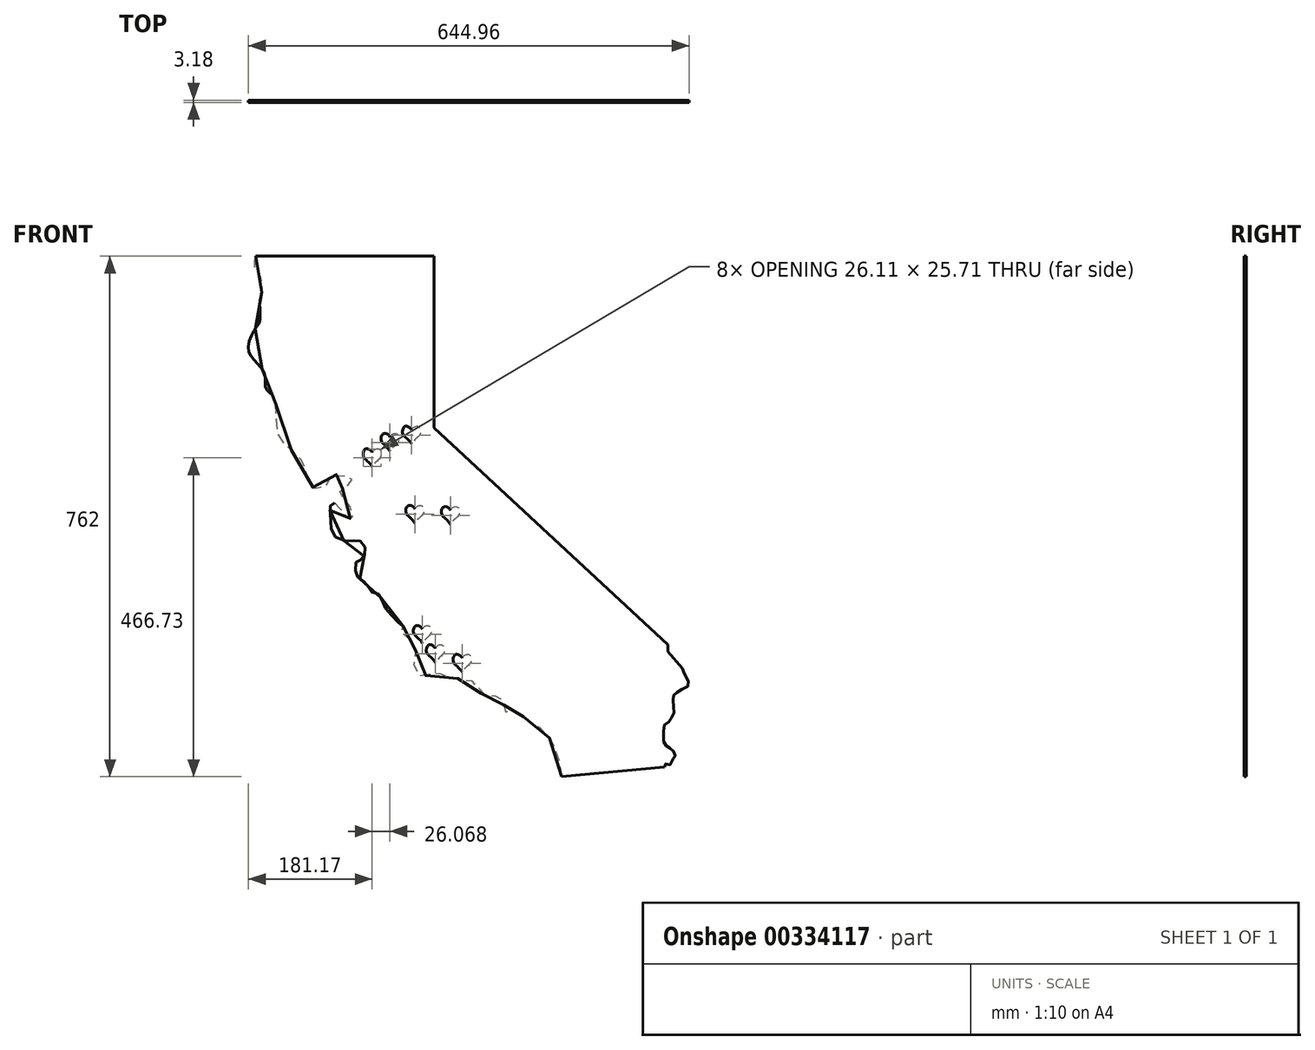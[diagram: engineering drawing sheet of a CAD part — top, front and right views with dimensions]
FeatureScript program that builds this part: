
annotation { "Feature Type Name" : "Feature", "Feature Type Description" : "" }
export const myFeature = defineFeature(function(context is Context, id is Id, definition is map)
    precondition{}
    {
        {
            var Q0;
            Q0=qCreatedBy(makeId("Front.planeOp"),FACE);
            var sketch = newSketch(context, id + "F0", { "sketchPlane" : qUnion([Q0])});
            skPoint(sketch, "E0.middle", {"position": v(0, 0) * mm});
            skLineSegment(sketch, "E1", {"start": v(-635.46, 762) * mm, "end": v(-374.52, 762) * mm});
            skLineSegment(sketch, "E2", {"start": v(-374.52, 762) * mm, "end": v(-374.52, 510.67) * mm});
            skLineSegment(sketch, "E3", {"start": v(-374.52, 510.67) * mm, "end": v(-32.38, 193.27) * mm});
            skLineSegment(sketch, "E4", {"start": v(-32.38, 193.27) * mm, "end": v(-32.38, 183.1) * mm});
            skLineSegment(sketch, "E5", {"start": v(-32.38, 183.1) * mm, "end": v(-11.17, 158.91) * mm});
            skLineSegment(sketch, "E6", {"start": v(-187.52, 0) * mm, "end": v(-37.43, 13.95) * mm});
            skFitSpline(sketch, "E7", {"points": [v(-37.43, 13.95) * mm, v(-37.43, 16.64) * mm, v(-36.79, 17.86) * mm, v(-35.5, 18.8) * mm, v(-33.12, 18.04) * mm, v(-29.91, 17.05) * mm, v(-28.22, 17.8) * mm, v(-27.06, 19.09) * mm, v(-26.77, 21.7) * mm, v(-26.53, 23.34) * mm, v(-25.54, 24.33) * mm, v(-24.32, 25.09) * mm, v(-24.26, 26.31) * mm, v(-23.27, 27.77) * mm, v(-22.16, 28.93) * mm, v(-21.58, 30.1) * mm, v(-21.46, 32.78) * mm, v(-22.16, 34.53) * mm, v(-25.08, 38.78) * mm, v(-27.64, 41.63) * mm, v(-30.38, 42.1) * mm, v(-32.18, 43.9) * mm, v(-34.28, 45.3) * mm, v(-35.62, 45.54) * mm, v(-37.43, 47.52) * mm, v(-38.3, 53.58) * mm, v(-38.36, 67.79) * mm, v(-37.95, 72.92) * mm, v(-36.67, 76.35) * mm, v(-34.46, 78.1) * mm, v(-30.96, 80.08) * mm, v(-28.8, 82.94) * mm, v(-27.99, 85.2) * mm, v(-24.96, 87.6) * mm, v(-23.8, 91.5) * mm, v(-23.21, 97.1) * mm, v(-23.68, 101.23) * mm, v(-24.26, 105.71) * mm, v(-24.55, 111.07) * mm, v(-24.26, 115.27) * mm, v(-23.74, 117.6) * mm, v(-23.62, 119.52) * mm, v(-21.23, 122.67) * mm, v(-18.67, 123.3) * mm, v(-14.53, 127.1) * mm, v(-11.56, 127.97) * mm, v(-5.91, 130.7) * mm, v(-2.24, 132.69) * mm, v(-1.2, 136.42) * mm, v(-3.11, 142.24) * mm, v(-7.83, 150.22) * mm, v(-10.22, 155.3) * mm, v(-11.17, 158.91) * mm], "startDerivative": vector(-13.19, 172.42) * mm, "endDerivative": vector(-38.47, 173.9) * mm});
            skFitSpline(sketch, "E8", {"points": [v(-187.52, 0) * mm, v(-190.53, 20.29) * mm, v(-196.76, 40.63) * mm, v(-204.85, 55.58) * mm, v(-215.23, 67.41) * mm, v(-224.16, 74.68) * mm, v(-237.65, 81.32) * mm, v(-246.16, 91.08) * mm, v(-258.41, 100) * mm, v(-265.68, 93.57) * mm, v(-267.76, 92.74) * mm, v(-271.28, 100.22) * mm, v(-273.98, 113.3) * mm, v(-280.63, 116.62) * mm, v(-293.08, 119.52) * mm, v(-302, 120.15) * mm, v(-307, 124.3) * mm, v(-311.35, 135.92) * mm, v(-320.9, 139.66) * mm, v(-329.83, 139.87) * mm, v(-341.25, 144.23) * mm, v(-355.36, 145.47) * mm, v(-367.82, 151.08) * mm, v(-381.52, 149.63) * mm, v(-389.83, 147.13) * mm, v(-396.88, 148.38) * mm, v(-403.32, 161.87) * mm, v(-401.87, 176.4) * mm, v(-404.57, 195.71) * mm, v(-418.9, 206.72) * mm, v(-420.97, 212.11) * mm, v(-417.85, 214.81) * mm, v(-421.17, 222.08) * mm, v(-426.16, 225.2) * mm, v(-441.52, 241.8) * mm, v(-448.64, 252.16) * mm, v(-454.7, 266.6) * mm, v(-463.56, 268.94) * mm, v(-469.62, 275.46) * mm, v(-472.88, 281.99) * mm, v(-485, 291.3) * mm, v(-488.72, 297.83) * mm, v(-488.72, 313.21) * mm, v(-485, 315.54) * mm, v(-479.4, 318.8) * mm, v(-474.74, 329.06) * mm, v(-478.94, 342.58) * mm, v(-489.2, 345.84) * mm, v(-498.51, 344.44) * mm, v(-520.88, 352.36) * mm, v(-525.54, 369.14) * mm, v(-525.54, 379.4) * mm, v(-526.94, 392.44) * mm, v(-522.75, 401.3) * mm, v(-514.36, 396.64) * mm, v(-508.3, 385.92) * mm, v(-494.78, 378) * mm, v(-496.18, 392.9) * mm, v(-508.3, 408.29) * mm, v(-511.56, 418.08) * mm, v(-495.72, 430.2) * mm, v(-494.78, 435.79) * mm, v(-505.04, 439.51) * mm, v(-514.36, 439.51) * mm, v(-519.48, 443.7) * mm, v(-526, 440.45) * mm, v(-527.87, 433.46) * mm, v(-537.2, 422.27) * mm, v(-555.84, 426.93) * mm, v(-562.83, 451.63) * mm, v(-570.28, 465.61) * mm, v(-591.26, 485.65) * mm, v(-602.44, 501.5) * mm, v(-606.17, 542.98) * mm, v(-611.3, 559.29) * mm, v(-620.62, 568.61) * mm, v(-622.02, 587.72) * mm, v(-635.53, 607.76) * mm, v(-645.95, 624.54) * mm, v(-638.8, 651.1) * mm, v(-629.47, 666.95) * mm, v(-629.47, 688.39) * mm, v(-628.07, 701.9) * mm, v(-626.21, 721.94) * mm, v(-633.2, 740.58) * mm, v(-636.46, 744.31) * mm, v(-635.46, 762) * mm], "startDerivative": vector(-159.4, 1384.08) * mm, "endDerivative": vector(241.74, 1617.9) * mm});
            skSolve(sketch);
        }
        {
            var Q0;
            Q0 = qSketchRegion(id + "F0", true);
            extrude(context, id + "F1", {"entities" : qUnion([Q0]), "depth" : 3.17 * mm});
        }
        {
            var Q0;
            Q0=makeQuery(id+"F1.opExtrude","CAP_FACE",FACE,{"disambiguationData":[OSD([sQuery(id+"F0.wireOp",EDGE,"E1"),sQuery(id+"F0.wireOp",EDGE,"E2"),sQuery(id+"F0.wireOp",EDGE,"E3"),sQuery(id+"F0.wireOp",EDGE,"E4"),sQuery(id+"F0.wireOp",EDGE,"E5"),sQuery(id+"F0.wireOp",EDGE,"E6"),sQuery(id+"F0.wireOp",EDGE,"E7"),sQuery(id+"F0.wireOp",EDGE,"E8")])],"isStart":false});
            var sketch = newSketch(context, id + "F2", { "sketchPlane" : qUnion([Q0])});
            skLineSegment(sketch, "E9.bottom", {"start": v(-451.6, 501.86) * mm, "end": v(-426.2, 501.86) * mm, "construction": true});
            skLineSegment(sketch, "E9.top", {"start": v(-451.6, 476.46) * mm, "end": v(-426.2, 476.46) * mm, "construction": true});
            skLineSegment(sketch, "E9.left", {"start": v(-451.6, 501.86) * mm, "end": v(-451.6, 476.46) * mm, "construction": true});
            skLineSegment(sketch, "E9.right", {"start": v(-426.2, 501.86) * mm, "end": v(-426.2, 476.46) * mm, "construction": true});
            skPoint(sketch, "E9.middle", {"position": v(-438.9, 489.16) * mm});
            skLineSegment(sketch, "E10", {"start": v(-438.9, 501.86) * mm, "end": v(-438.9, 476.46) * mm, "construction": true});
            skFitSpline(sketch, "E11", {"points": [v(-438.9, 496.92) * mm, v(-435.63, 501.1) * mm, v(-428.7, 501.86) * mm, v(-426.2, 491.22) * mm, v(-438.9, 476.46) * mm], "startDerivative": vector(12.4, 24.02) * mm, "endDerivative": vector(-33.58, -61.2) * mm});
            skFitSpline(sketch, "E12.MirrorCS", {"points": [v(-438.9, 496.92) * mm, v(-442.18, 501.1) * mm, v(-449.1, 501.86) * mm, v(-451.6, 491.22) * mm, v(-438.9, 476.46) * mm], "startDerivative": vector(-12.4, 24.02) * mm, "endDerivative": vector(33.58, -61.2) * mm});
            skLineSegment(sketch, "E13.bottom", {"start": v(-477.67, 479.27) * mm, "end": v(-452.27, 479.27) * mm, "construction": true});
            skLineSegment(sketch, "E13.top", {"start": v(-477.67, 453.87) * mm, "end": v(-452.27, 453.87) * mm, "construction": true});
            skLineSegment(sketch, "E13.left", {"start": v(-477.67, 479.27) * mm, "end": v(-477.67, 453.87) * mm, "construction": true});
            skLineSegment(sketch, "E13.right", {"start": v(-452.27, 479.27) * mm, "end": v(-452.27, 453.87) * mm, "construction": true});
            skPoint(sketch, "E13.middle", {"position": v(-464.97, 466.57) * mm});
            skLineSegment(sketch, "E14", {"start": v(-464.97, 479.27) * mm, "end": v(-464.97, 453.87) * mm, "construction": true});
            skFitSpline(sketch, "E15", {"points": [v(-464.97, 474.33) * mm, v(-461.7, 478.5) * mm, v(-454.77, 479.27) * mm, v(-452.27, 468.63) * mm, v(-464.97, 453.87) * mm], "startDerivative": vector(12.4, 24.02) * mm, "endDerivative": vector(-33.58, -61.2) * mm});
            skFitSpline(sketch, "E16.MirrorCS", {"points": [v(-464.97, 474.33) * mm, v(-468.24, 478.5) * mm, v(-475.17, 479.27) * mm, v(-477.67, 468.63) * mm, v(-464.97, 453.87) * mm], "startDerivative": vector(-12.4, 24.02) * mm, "endDerivative": vector(33.58, -61.2) * mm});
            skLineSegment(sketch, "E17.bottom", {"start": v(-420.03, 512.35) * mm, "end": v(-394.63, 512.35) * mm, "construction": true});
            skLineSegment(sketch, "E17.top", {"start": v(-420.03, 486.95) * mm, "end": v(-394.63, 486.95) * mm, "construction": true});
            skLineSegment(sketch, "E17.left", {"start": v(-420.03, 512.35) * mm, "end": v(-420.03, 486.95) * mm, "construction": true});
            skLineSegment(sketch, "E17.right", {"start": v(-394.63, 512.35) * mm, "end": v(-394.63, 486.95) * mm, "construction": true});
            skPoint(sketch, "E17.middle", {"position": v(-407.33, 499.65) * mm});
            skLineSegment(sketch, "E18", {"start": v(-407.33, 512.35) * mm, "end": v(-407.33, 486.95) * mm, "construction": true});
            skFitSpline(sketch, "E19", {"points": [v(-407.33, 507.41) * mm, v(-404.06, 511.59) * mm, v(-397.13, 512.35) * mm, v(-394.63, 501.71) * mm, v(-407.33, 486.95) * mm], "startDerivative": vector(12.4, 24.02) * mm, "endDerivative": vector(-33.58, -61.2) * mm});
            skFitSpline(sketch, "E20.MirrorCS", {"points": [v(-407.33, 507.41) * mm, v(-410.6, 511.59) * mm, v(-417.53, 512.35) * mm, v(-420.03, 501.71) * mm, v(-407.33, 486.95) * mm], "startDerivative": vector(-12.4, 24.02) * mm, "endDerivative": vector(33.58, -61.2) * mm});
            skLineSegment(sketch, "E21.bottom", {"start": v(-415.26, 396.53) * mm, "end": v(-389.86, 396.53) * mm, "construction": true});
            skLineSegment(sketch, "E21.top", {"start": v(-415.26, 371.13) * mm, "end": v(-389.86, 371.13) * mm, "construction": true});
            skLineSegment(sketch, "E21.left", {"start": v(-415.26, 396.53) * mm, "end": v(-415.26, 371.13) * mm, "construction": true});
            skLineSegment(sketch, "E21.right", {"start": v(-389.86, 396.53) * mm, "end": v(-389.86, 371.13) * mm, "construction": true});
            skPoint(sketch, "E21.middle", {"position": v(-402.56, 383.83) * mm});
            skLineSegment(sketch, "E22", {"start": v(-402.56, 396.53) * mm, "end": v(-402.56, 371.13) * mm, "construction": true});
            skFitSpline(sketch, "E23", {"points": [v(-402.56, 391.59) * mm, v(-399.29, 395.76) * mm, v(-392.37, 396.53) * mm, v(-389.86, 385.89) * mm, v(-402.56, 371.13) * mm], "startDerivative": vector(12.4, 24.02) * mm, "endDerivative": vector(-33.58, -61.2) * mm});
            skFitSpline(sketch, "E24.MirrorCS", {"points": [v(-402.56, 391.59) * mm, v(-405.84, 395.76) * mm, v(-412.76, 396.53) * mm, v(-415.26, 385.89) * mm, v(-402.56, 371.13) * mm], "startDerivative": vector(-12.4, 24.02) * mm, "endDerivative": vector(33.58, -61.2) * mm});
            skLineSegment(sketch, "E25.bottom", {"start": v(-363.2, 394.75) * mm, "end": v(-337.8, 394.75) * mm, "construction": true});
            skLineSegment(sketch, "E25.top", {"start": v(-363.2, 369.35) * mm, "end": v(-337.8, 369.35) * mm, "construction": true});
            skLineSegment(sketch, "E25.left", {"start": v(-363.2, 394.75) * mm, "end": v(-363.2, 369.35) * mm, "construction": true});
            skLineSegment(sketch, "E25.right", {"start": v(-337.8, 394.75) * mm, "end": v(-337.8, 369.35) * mm, "construction": true});
            skPoint(sketch, "E25.middle", {"position": v(-350.5, 382.05) * mm});
            skLineSegment(sketch, "E26", {"start": v(-350.5, 394.75) * mm, "end": v(-350.5, 369.35) * mm, "construction": true});
            skFitSpline(sketch, "E27", {"points": [v(-350.5, 389.8) * mm, v(-347.23, 393.98) * mm, v(-340.3, 394.75) * mm, v(-337.8, 384.1) * mm, v(-350.5, 369.35) * mm], "startDerivative": vector(12.4, 24.02) * mm, "endDerivative": vector(-33.58, -61.2) * mm});
            skFitSpline(sketch, "E28.MirrorCS", {"points": [v(-350.5, 389.8) * mm, v(-353.78, 393.98) * mm, v(-360.7, 394.75) * mm, v(-363.2, 384.1) * mm, v(-350.5, 369.35) * mm], "startDerivative": vector(-12.4, 24.02) * mm, "endDerivative": vector(33.58, -61.2) * mm});
            skLineSegment(sketch, "E29.bottom", {"start": v(-404.27, 220.64) * mm, "end": v(-378.87, 220.64) * mm, "construction": true});
            skLineSegment(sketch, "E29.top", {"start": v(-404.27, 195.24) * mm, "end": v(-378.87, 195.24) * mm, "construction": true});
            skLineSegment(sketch, "E29.left", {"start": v(-404.27, 220.64) * mm, "end": v(-404.27, 195.24) * mm, "construction": true});
            skLineSegment(sketch, "E29.right", {"start": v(-378.87, 220.64) * mm, "end": v(-378.87, 195.24) * mm, "construction": true});
            skPoint(sketch, "E29.middle", {"position": v(-391.57, 207.94) * mm});
            skLineSegment(sketch, "E30", {"start": v(-391.57, 220.64) * mm, "end": v(-391.57, 195.24) * mm, "construction": true});
            skFitSpline(sketch, "E31", {"points": [v(-391.57, 215.7) * mm, v(-388.3, 219.87) * mm, v(-381.38, 220.64) * mm, v(-378.87, 210) * mm, v(-391.57, 195.24) * mm], "startDerivative": vector(12.4, 24.02) * mm, "endDerivative": vector(-33.58, -61.2) * mm});
            skFitSpline(sketch, "E32.MirrorCS", {"points": [v(-391.57, 215.7) * mm, v(-394.85, 219.87) * mm, v(-401.77, 220.64) * mm, v(-404.27, 210) * mm, v(-391.57, 195.24) * mm], "startDerivative": vector(-12.4, 24.02) * mm, "endDerivative": vector(33.58, -61.2) * mm});
            skLineSegment(sketch, "E33.bottom", {"start": v(-385.22, 192.45) * mm, "end": v(-359.82, 192.45) * mm, "construction": true});
            skLineSegment(sketch, "E33.top", {"start": v(-385.22, 167.05) * mm, "end": v(-359.82, 167.05) * mm, "construction": true});
            skLineSegment(sketch, "E33.left", {"start": v(-385.22, 192.45) * mm, "end": v(-385.22, 167.05) * mm, "construction": true});
            skLineSegment(sketch, "E33.right", {"start": v(-359.82, 192.45) * mm, "end": v(-359.82, 167.05) * mm, "construction": true});
            skPoint(sketch, "E33.middle", {"position": v(-372.52, 179.75) * mm});
            skLineSegment(sketch, "E34", {"start": v(-372.52, 192.45) * mm, "end": v(-372.52, 167.05) * mm, "construction": true});
            skFitSpline(sketch, "E35", {"points": [v(-372.52, 187.51) * mm, v(-369.24, 191.69) * mm, v(-362.32, 192.45) * mm, v(-359.82, 181.81) * mm, v(-372.52, 167.05) * mm], "startDerivative": vector(12.4, 24.02) * mm, "endDerivative": vector(-33.58, -61.2) * mm});
            skFitSpline(sketch, "E36.MirrorCS", {"points": [v(-372.52, 187.51) * mm, v(-375.8, 191.69) * mm, v(-382.71, 192.45) * mm, v(-385.22, 181.81) * mm, v(-372.52, 167.05) * mm], "startDerivative": vector(-12.4, 24.02) * mm, "endDerivative": vector(33.58, -61.2) * mm});
            skLineSegment(sketch, "E37.bottom", {"start": v(-346.09, 178.35) * mm, "end": v(-320.69, 178.35) * mm, "construction": true});
            skLineSegment(sketch, "E37.top", {"start": v(-346.09, 152.95) * mm, "end": v(-320.69, 152.95) * mm, "construction": true});
            skLineSegment(sketch, "E37.left", {"start": v(-346.09, 178.35) * mm, "end": v(-346.09, 152.95) * mm, "construction": true});
            skLineSegment(sketch, "E37.right", {"start": v(-320.69, 178.35) * mm, "end": v(-320.69, 152.95) * mm, "construction": true});
            skPoint(sketch, "E37.middle", {"position": v(-333.39, 165.65) * mm});
            skLineSegment(sketch, "E38", {"start": v(-333.39, 178.35) * mm, "end": v(-333.39, 152.95) * mm, "construction": true});
            skFitSpline(sketch, "E39", {"points": [v(-333.39, 173.4) * mm, v(-330.11, 177.58) * mm, v(-323.2, 178.35) * mm, v(-320.69, 167.7) * mm, v(-333.39, 152.95) * mm], "startDerivative": vector(12.4, 24.02) * mm, "endDerivative": vector(-33.58, -61.2) * mm});
            skFitSpline(sketch, "E40.MirrorCS", {"points": [v(-333.39, 173.4) * mm, v(-336.66, 177.58) * mm, v(-343.58, 178.35) * mm, v(-346.09, 167.7) * mm, v(-333.39, 152.95) * mm], "startDerivative": vector(-12.4, 24.02) * mm, "endDerivative": vector(33.58, -61.2) * mm});
            skSolve(sketch);
        }
        {
            var Q0;
            Q0 = qSketchRegion(id + "F2", true);
            extrude(context, id + "F3", {"entities" : qUnion([Q0]), "operationType" : NewBodyOperationType.REMOVE, "endBound" : BoundingType.THROUGH_ALL, "oppositeDirection" : true, "depth" : 25.4 * mm});
        }
    });
